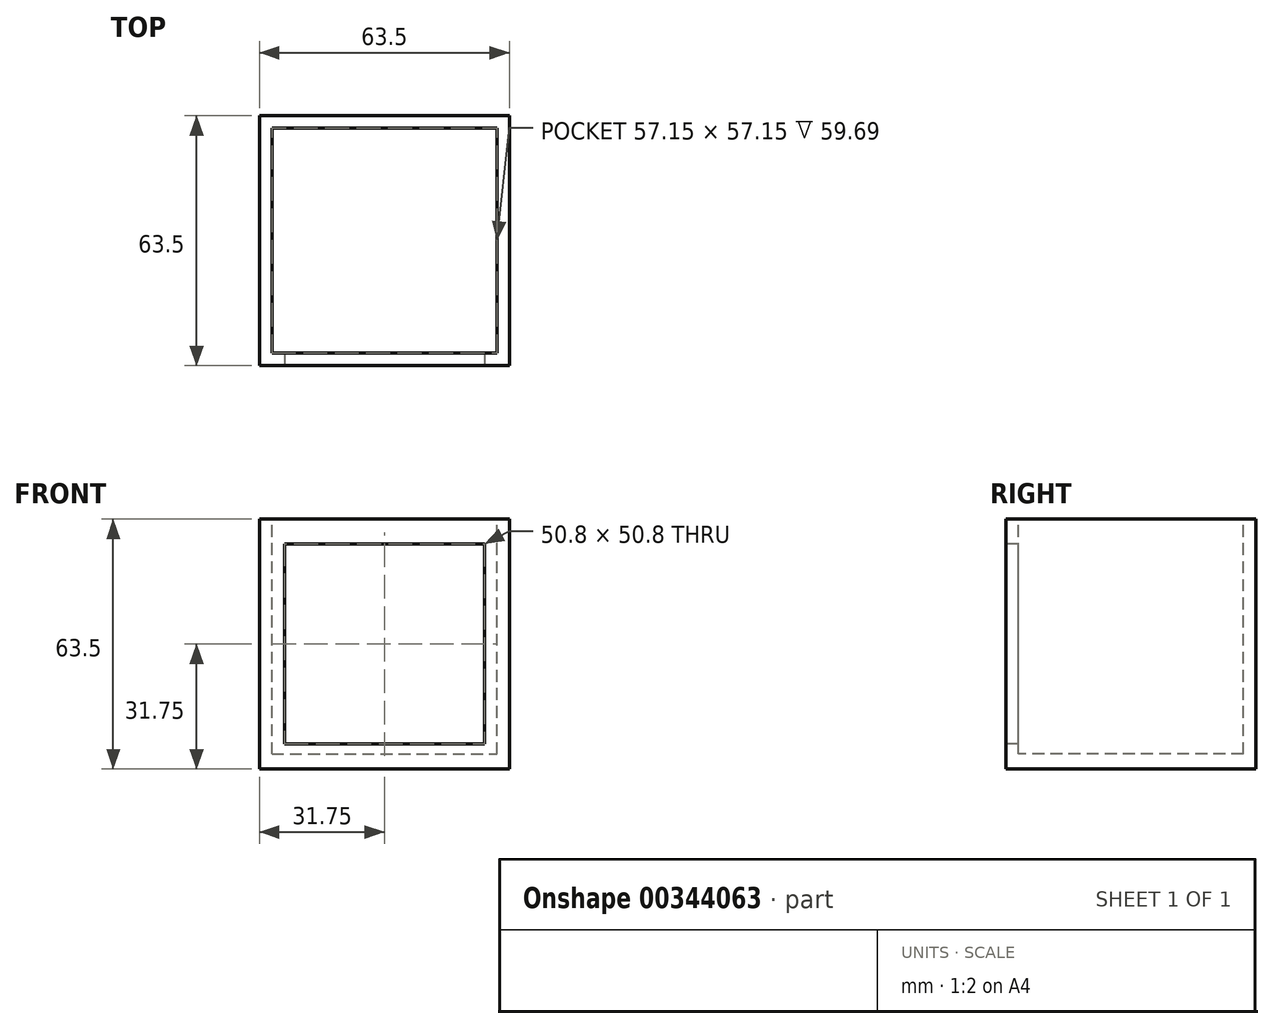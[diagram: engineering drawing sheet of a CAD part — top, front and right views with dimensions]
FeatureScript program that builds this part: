
annotation { "Feature Type Name" : "Feature", "Feature Type Description" : "" }
export const myFeature = defineFeature(function(context is Context, id is Id, definition is map)
    precondition{}
    {
        {
            var Q0;
            Q0=qCreatedBy(makeId("Top.planeOp"),FACE);
            var sketch = newSketch(context, id + "F0", { "sketchPlane" : qUnion([Q0])});
            skLineSegment(sketch, "E0.bottom", {"start": v(31.75, 31.75) * mm, "end": v(-31.75, 31.75) * mm});
            skLineSegment(sketch, "E0.top", {"start": v(31.75, -31.75) * mm, "end": v(-31.75, -31.75) * mm});
            skLineSegment(sketch, "E0.left", {"start": v(31.75, 31.75) * mm, "end": v(31.75, -31.75) * mm});
            skLineSegment(sketch, "E0.right", {"start": v(-31.75, 31.75) * mm, "end": v(-31.75, -31.75) * mm});
            skPoint(sketch, "E0.middle", {"position": v(0, 0) * mm});
            skSolve(sketch);
        }
        {
            var Q0;
            Q0=makeQuery(id+"F0.imprint","IMPRINT",FACE,{"disambiguationData":[TD([[makeQuery(id+"F0.imprint","IMPRINT",EDGE,{"derivedFrom":sQuery(id+"F0.wireOp",EDGE,"E0.bottom")}),1.0]])]});
            extrude(context, id + "F1", {"entities" : qUnion([Q0]), "depth" : 63.5 * mm});
        }
        {
            var Q0;
            Q0=makeQuery(id+"F1.opExtrude","SWEPT_FACE",FACE,{"disambiguationData":[OSD([sQuery(id+"F0.wireOp",EDGE,"E0.top")])]});
            var sketch = newSketch(context, id + "F2", { "sketchPlane" : qUnion([Q0])});
            skLineSegment(sketch, "E1.bottom", {"start": v(25.4, 57.15) * mm, "end": v(-25.4, 57.15) * mm});
            skLineSegment(sketch, "E1.top", {"start": v(25.4, 6.35) * mm, "end": v(-25.4, 6.35) * mm});
            skLineSegment(sketch, "E1.left", {"start": v(25.4, 57.15) * mm, "end": v(25.4, 6.35) * mm});
            skLineSegment(sketch, "E1.right", {"start": v(-25.4, 57.15) * mm, "end": v(-25.4, 6.35) * mm});
            skPoint(sketch, "E1.middle", {"position": v(0, 31.75) * mm});
            skPoint(sketch, "E1.middle.positionSnap0", {"position": v(-31.75, 31.75) * mm});
            skPoint(sketch, "E1.centerSnap0", {"position": v(-31.75, 31.75) * mm});
            skSolve(sketch);
        }
        {
            var Q0;
            Q0=makeQuery(id+"F2.imprint","IMPRINT",FACE,{"disambiguationData":[TD([[makeQuery(id+"F2.imprint","IMPRINT",EDGE,{"derivedFrom":sQuery(id+"F2.wireOp",EDGE,"E1.bottom")}),1.0]])]});
            extrude(context, id + "F3", {"entities" : qUnion([Q0]), "operationType" : NewBodyOperationType.REMOVE, "oppositeDirection" : true, "depth" : 57.15 * mm});
        }
        {
            var Q0;
            Q0=makeQuery(id+"F1.opExtrude","CAP_FACE",FACE,{"disambiguationData":[OSD([sQuery(id+"F0.wireOp",EDGE,"E0.bottom"),sQuery(id+"F0.wireOp",EDGE,"E0.top"),sQuery(id+"F0.wireOp",EDGE,"E0.left"),sQuery(id+"F0.wireOp",EDGE,"E0.right")])],"isStart":false});
            var sketch = newSketch(context, id + "F4", { "sketchPlane" : qUnion([Q0])});
            skLineSegment(sketch, "E2.bottom", {"start": v(-28.57, 28.57) * mm, "end": v(28.58, 28.57) * mm});
            skLineSegment(sketch, "E2.top", {"start": v(-28.58, -28.57) * mm, "end": v(28.57, -28.57) * mm});
            skLineSegment(sketch, "E2.left", {"start": v(-28.57, 28.57) * mm, "end": v(-28.58, -28.57) * mm});
            skLineSegment(sketch, "E2.right", {"start": v(28.58, 28.58) * mm, "end": v(28.57, -28.57) * mm});
            skPoint(sketch, "E2.middle", {"position": v(0, 0) * mm});
            skSolve(sketch);
        }
        {
            var Q0;
            Q0=makeQuery(id+"F4.imprint","IMPRINT",FACE,{"disambiguationData":[TD([[makeQuery(id+"F4.imprint","IMPRINT",EDGE,{"derivedFrom":sQuery(id+"F4.wireOp",EDGE,"E2.bottom")}),-1.0]])]});
            extrude(context, id + "F5", {"entities" : qUnion([Q0]), "operationType" : NewBodyOperationType.REMOVE, "oppositeDirection" : true, "depth" : 59.69 * mm});
        }
    });
